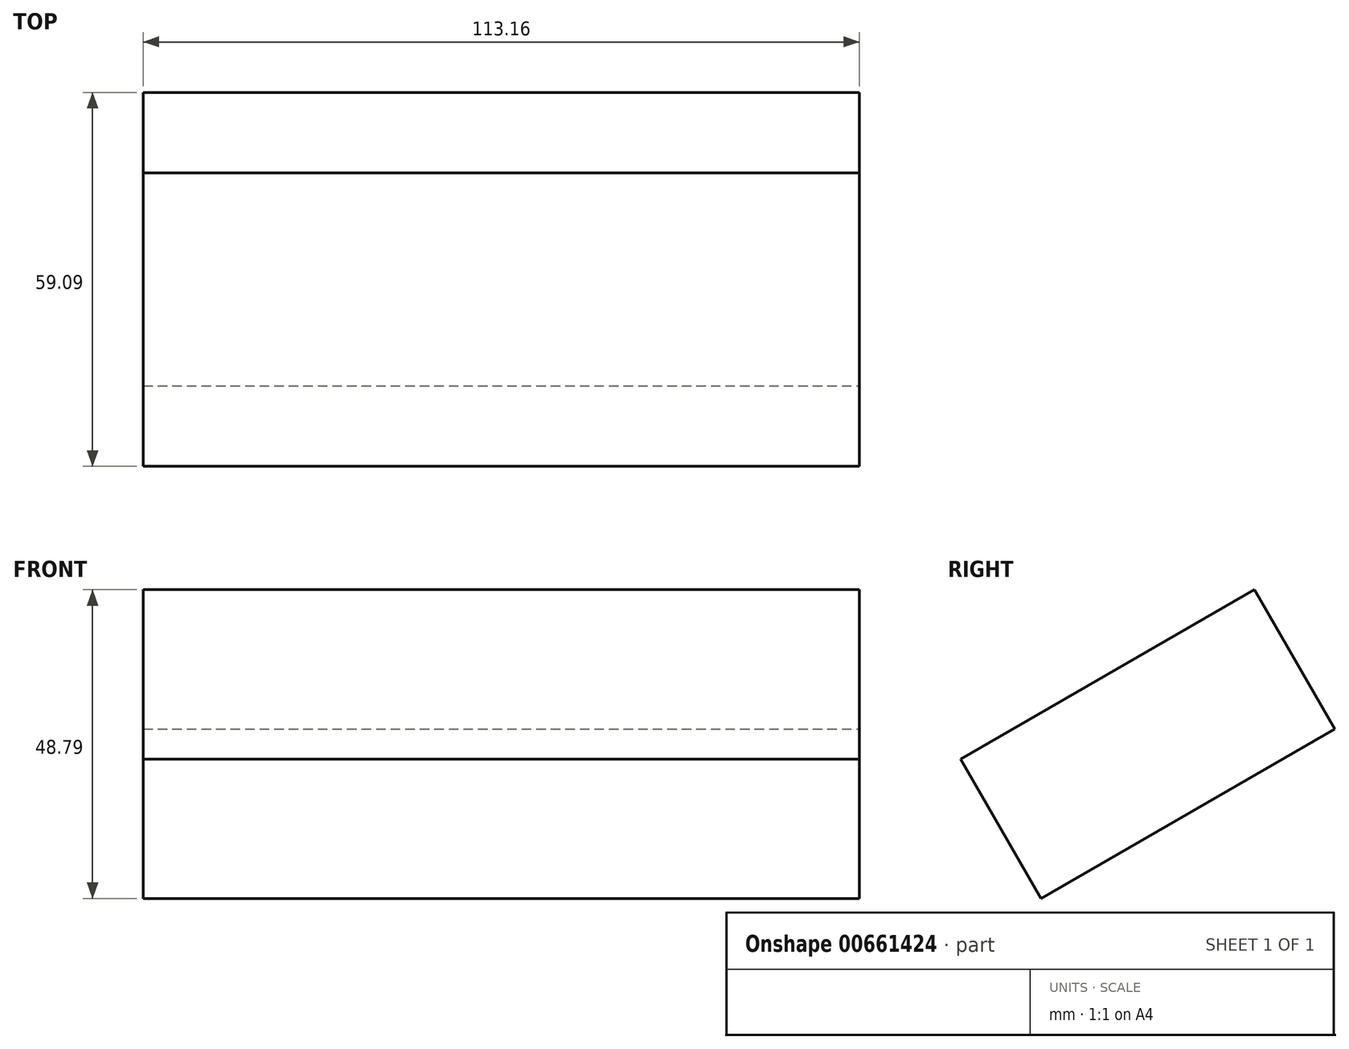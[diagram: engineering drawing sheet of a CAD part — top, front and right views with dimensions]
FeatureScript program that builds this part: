
annotation { "Feature Type Name" : "Feature", "Feature Type Description" : "" }
export const myFeature = defineFeature(function(context is Context, id is Id, definition is map)
    precondition{}
    {
        {
            var Q0;
            Q0=qCreatedBy(makeId("Top.planeOp"),FACE);
            var sketch = newSketch(context, id + "F0", { "sketchPlane" : qUnion([Q0])});
            skLineSegment(sketch, "E0.bottom", {"start": v(-64.2, 28.38) * mm, "end": v(48.96, 28.38) * mm});
            skLineSegment(sketch, "E0.top", {"start": v(-64.2, -25.2) * mm, "end": v(48.96, -25.2) * mm});
            skLineSegment(sketch, "E0.left", {"start": v(-64.2, 28.38) * mm, "end": v(-64.2, -25.2) * mm});
            skLineSegment(sketch, "E0.right", {"start": v(48.96, 28.38) * mm, "end": v(48.96, -25.2) * mm});
            skSolve(sketch);
        }
        {
            var Q0;
            Q0 = qSketchRegion(id + "F0", true);
            extrude(context, id + "F1", {"entities" : qUnion([Q0]), "depth" : 25.4 * mm, "offsetDistance" : 25.4 * mm});
        }
        {
            var Q0;
            Q0=makeQuery(id+"F1.opExtrude","SWEPT_BODY",BODY,{"disambiguationData":[OSD([sQuery(id+"F0.wireOp",EDGE,"E0.bottom"),sQuery(id+"F0.wireOp",EDGE,"E0.top"),sQuery(id+"F0.wireOp",EDGE,"E0.left"),sQuery(id+"F0.wireOp",EDGE,"E0.right")])]});
            var Q1;
            Q1=makeQuery(id+"F1.opExtrude","CAP_EDGE",EDGE,{"disambiguationData":[OSD([sQuery(id+"F0.wireOp",EDGE,"E0.top")])],"isStart":false});
            transform(context, id + "F2", {"entities" : qUnion([Q0]), "transformType" : TransformType.ROTATION, "transformAxis" : qUnion([Q1]), "angle" : 30 * degree, "makeCopy" : false});
        }
    });
